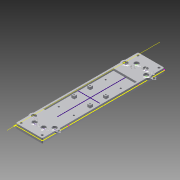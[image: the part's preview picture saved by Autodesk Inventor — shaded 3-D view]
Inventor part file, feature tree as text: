
AUTODESK INVENTOR PART (.ipt)
format: ipt  version: 2015 (Build 190159000, 159)  size: 313,344 bytes
history: native  units: mm
features: sketch x14, extrude x7, reference x5, mirror x4, plane x3, hole x1, revolve x1, fillet x1
ambient origin geometry x8: Origin, YZ Plane, XZ Plane, XY Plane, X Axis, Y Axis, Z Axis, Center Point
bodies: Solid1 (feature_tree)
feature tree (36):
  extrude  "Extrusion1"  Depth=235.0mm
  sketch  "Sketch3"  dims[d2=5.0mm d3=0.0mm d8=90.0deg]
  plane  "Work Plane1"
  plane  "Work Plane2"
  sketch  "Sketch4"  dims[d9=90.0deg d10=4.2mm]
  extrude  "Extrusion8"  TaperAngle=90.0deg  [1 undecoded]
  hole  "Hole1"  [1 undecoded]
  sketch  "Sketch10"  dims[d15=4.2mm d16=4.2mm]
  sketch  "Sketch11"  dims[d17=4.2mm d36=36.0mm]
  extrude  "Extrusion9"  Depth=4.2mm
  mirror  "Mirror5"
  mirror  "Mirror6"
  extrude  "Extrusion11"  Depth=4.2mm
  extrude  "Extrusion12"  Depth=4.2mm
  plane  "Work Plane5"
  sketch  "Sketch18"  dims[d52=3.0mm]
  revolve  "Revolution1"  [1 undecoded]
  mirror  "Mirror7"
  mirror  "Mirror8"
  extrude  "Extrusion13"  Depth=30.5mm
  extrude  "Extrusion14"  Depth=5.0mm TaperAngle=0.0deg
  fillet  "Fillet3"  Radius=3.0mm
  sketch  "Sketch1"  dims[d0=51.0mm d1=235.0mm]
  sketch  "Sketch8"  dims[d11=4.2mm d12=4.2mm]
  sketch  "Sketch9"  dims[d13=4.2mm d14=4.2mm]
  sketch  "Sketch12"  dims[d37=36.0mm d38=30.5mm]
  sketch  "Sketch15"  dims[d39=30.5mm d40=5.0mm d41=0.0mm]
  sketch  "Sketch16"  dims[d42=2.616mm d43=6.0mm d44=4.0mm d45=2.0mm d46=90.0deg d47=5.0mm d48=0.0mm d51=3.0mm]
  sketch  "Sketch19"  dims[d53=4.0mm d54=0.0mm]
  reference  "Reference10"
  sketch  "Sketch20"  dims[d78=8.5mm]
  reference  "Reference11"
  reference  "Reference12"
  reference  "Reference13"
  reference  "Reference14"
  sketch  "Sketch21"  dims[d79=8.5mm d80=8.5mm d81=8.5mm d82=8.5mm d83=8.5mm d84=8.5mm d85=8.5mm d86=5.625mm d87=29.5mm d88=19.5mm d89=16.875mm d90=4.2mm d91=4.2mm d92=19.5mm d93=16.875mm d94=5.625mm d95=29.5mm d96=5.625mm d97=29.5mm d98=19.5mm d99=16.875mm d100=19.5mm d101=16.875mm d102=5.625mm d103=29.5mm d104=4.2mm d105=4.2mm d106=4.2mm d107=4.2mm d108=15.0mm d109=15.0mm d110=15.0mm d111=15.0mm d112=4.0mm d113=0.0mm d115=4.2mm d116=4.2mm d117=4.2mm d118=4.2mm d119=5.625mm d120=29.5mm d121=19.5mm d122=34.125mm d123=19.5mm d124=16.875mm d125=4.2mm d126=4.2mm d127=5.625mm d128=29.5mm d129=4.2mm d130=4.2mm d131=5.625mm d132=29.5mm d133=19.5mm d134=34.125mm d135=19.5mm d136=16.875mm d137=5.625mm d138=29.5mm d139=5.0mm d140=0.0mm d143=45.0deg d145=90.0deg d146=5.0mm d147=0.0mm d150=4.2mm d153=5.2mm d154=5.2mm d155=9.0mm d156=0.0mm d157=2.0mm]
note: 3 required parameter values undecoded (feature->parameter linkage not recoverable at this tier; creation-order binding heuristic only, values carry confidence <= 0.55)